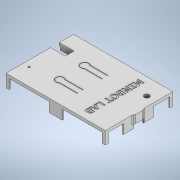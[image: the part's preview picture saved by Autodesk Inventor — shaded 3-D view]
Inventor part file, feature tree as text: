
AUTODESK INVENTOR PART (.ipt)
format: ipt  version: 2020 (Build 240168000, 168)  size: 748,032 bytes
history: native  units: mm
features: extrude x19, sketch x18, projected_geometry x7, fillet x5
ambient origin geometry x8: Origin, YZ Plane, XZ Plane, XY Plane, X Axis, Y Axis, Z Axis, Center Point
bodies: Solid1 (feature_tree)
feature tree (49):
  sketch  "Sketch1"  dims[d0=96.9mm d1=65.9mm]
  extrude  "Extrusion1"  Depth=65.9mm
  extrude  "Extrusion2"  Depth=1.0mm
  sketch  "Sketch3"  dims[d5=3.0mm d6=3.0mm]
  extrude  "Extrusion3"  Depth=3.0mm
  extrude  "Extrusion4"  Depth=12.3mm TaperAngle=0.0deg
  extrude  "Extrusion5"  Depth=8.5mm
  extrude  "Extrusion6"  Depth=12.3mm TaperAngle=0.0deg
  sketch  "Sketch9"  dims[d20=7.0mm d22=0.5mm d24=3.0mm]
  extrude  "Extrusion7"  Depth=31.8mm
  extrude  "Extrusion8"  Depth=0.5mm
  fillet  "Fillet1"  Radius=3.0mm
  extrude  "Extrusion9"  Depth=20.0mm
  extrude  "Extrusion10"  Depth=0.5mm
  fillet  "Fillet2"  Radius=12.3mm
  extrude  "Extrusion11"  Depth=0.5mm
  extrude  "Extrusion12"  Depth=16.5mm
  fillet  "Fillet3"  Radius=11.0mm
  extrude  "Extrusion13"  Depth=1.0mm
  fillet  "Fillet4"  Radius=1.0mm
  extrude  "Extrusion14"  Depth=1.0mm
  extrude  "Extrusion15"  Depth=11.0mm TaperAngle=0.0deg
  extrude  "Extrusion16"  Depth=27.73mm
  extrude  "Extrusion17"  Depth=8.8mm
  extrude  "Extrusion18"  Depth=0.4mm
  fillet  "Fillet5"  Radius=10.0mm
  extrude  "Extrusion19"  Depth=0.4mm TaperAngle=0.0deg
  sketch  "Sketch2"  dims[d2=1.0mm d3=0.0mm d4=1.0mm]
  projected_geometry  "Projected Loop1"
  sketch  "Sketch4"  dims[d7=20.0mm d9=360.0deg d11=12.3mm d12=0.0mm]
  projected_geometry  "Projected Loop2"
  sketch  "Sketch5"  dims[d13=14.0mm d14=8.5mm]
  sketch  "Sketch7"  dims[d15=14.5mm d16=12.3mm d17=0.0mm]
  sketch  "Sketch8"  dims[d18=21.0mm d19=31.8mm]
  sketch  "Sketch10"  dims[d25=3.0mm d26=20.0mm]
  sketch  "Sketch11"  dims[d27=0.5mm d28=0.5mm d29=12.3mm d30=0.0mm]
  projected_geometry  "Projected Loop3"
  sketch  "Sketch12"  dims[d31=7.0mm d32=0.5mm d33=3.0mm d34=3.0mm d35=20.0mm d36=0.5mm d37=0.5mm d38=24.2mm d39=0.5mm]
  projected_geometry  "Projected Loop4"
  sketch  "Sketch13"  dims[d40=6.0mm d41=16.5mm d42=11.0mm d43=0.0mm]
  sketch  "Sketch14"  dims[d44=4.0mm d45=11.4mm d46=1.0mm]
  sketch  "Sketch15"  dims[d47=5.0mm d48=1.0mm]
  projected_geometry  "Projected Loop5"
  sketch  "Sketch16"  dims[d49=13.0mm d50=11.0mm d51=0.0mm]
  projected_geometry  "Projected Loop6"
  sketch  "Sketch17"  dims[d52=9.5mm d53=27.73mm]
  projected_geometry  "Projected Loop7"
  sketch  "Sketch18"  dims[d55=1.1mm d56=8.8mm]
  sketch  "Sketch19"  dims[d57=1.0mm d58=10.0mm d59=10.0mm d60=7.9mm d61=0.0mm d62=7.9mm d63=0.0mm d64=2.0mm d65=5.0mm d66=16.5mm d67=8.9mm d68=0.5mm d69=10.0mm d70=0.0mm d71=10.0mm d72=0.0mm d73=2.0mm d74=1.8mm d75=10.0mm d76=0.0mm d77=15.0mm d78=5.0mm d79=33.0mm d80=10.0mm d81=0.0mm d82=2.0mm d83=5.0mm d84=5.0mm d85=1.9mm d86=0.0mm d87=1.0mm d88=1.0mm d89=1.9mm d90=0.0mm d91=1.9mm d92=0.0mm d93=1.0mm d94=1.0mm d95=1.0mm d96=5.0mm d97=0.0mm d98=1.0mm d99=19.0mm d100=1.0mm d101=5.0mm d102=0.0mm d103=14.5mm d104=5.0mm d105=19.5mm d106=5.0mm d107=0.0mm d108=1.5mm d109=0.4mm d110=0.0mm d111=2.0mm]
